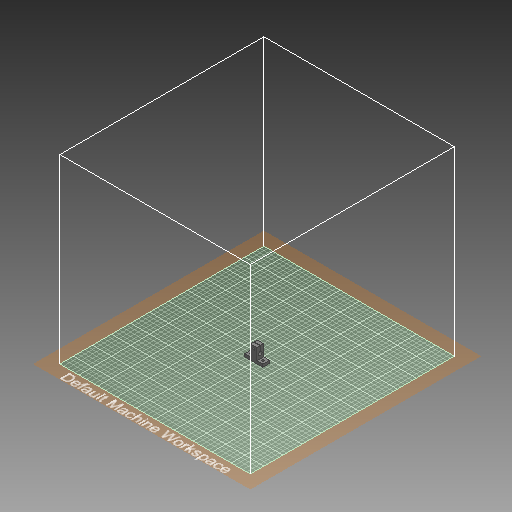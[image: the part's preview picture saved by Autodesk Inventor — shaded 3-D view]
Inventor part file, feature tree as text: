
AUTODESK INVENTOR PART (.ipt)
format: ipt  version: 2019 (Build 230136000, 136)  size: 347,136 bytes
history: native  units: in
note: dims shown in document units (in); Inventor stores cm internally (conversion verified against a paired STEP export)
features: sketch x9, extrude x8, other x3, reference x2
ambient origin geometry x8: Origin, YZ Plane, XZ Plane, XY Plane, X Axis, Y Axis, Z Axis, Center Point
bodies: Solid1 (feature_tree)
feature tree (22):
  extrude  "Extrusion1"  Depth=0.5906in
  extrude  "Extrusion2"  Depth=0.5512in
  extrude  "Extrusion4"  Depth=0.9843in
  extrude  "Extrusion5"  Depth=1.1811in TaperAngle=0.0deg
  extrude  "Extrusion6"  Depth=0.315in
  sketch  "Sketch7"  dims[d18=0.0394in d19=1.1811in d20=0.0in]
  sketch  "Sketch8"  dims[d21=0.1673in d22=0.2362in]
  extrude  "Extrusion8"  Depth=0.0394in TaperAngle=0.0deg
  extrude  "Extrusion9"  Depth=0.2362in
  sketch  "Sketch9"  dims[d23=1.1811in d24=0.0in d25=0.3937in]
  extrude  "Extrusion10"  Depth=0.3937in
  sketch  "Sketch1"  dims[d0=1.5748in d1=0.5906in]
  sketch  "Sketch2"  dims[d2=0.2362in d3=0.0in d4=0.5512in]
  sketch  "Sketch4"  dims[d5=0.9843in d6=0.0in d12=0.1673in]
  sketch  "Sketch5"  dims[d13=0.1673in d14=1.1811in d15=0.0in]
  sketch  "Sketch6"  dims[d16=0.315in d17=0.6299in]
  reference  "Reference1"
  reference  "Reference2"
  sketch  "Sketch10"  dims[d28=0.3937in d29=0.0in d30=0.3937in d31=0.0in d32=0.2362in d33=0.0591in d34=0.0in d35=0.2362in]
  other  "<userpath>\Stuff\Ajedrez2\Ajedrez2.iam"
  other  "Ajedrez2.iam"
  other  "Endstop mecânico - Chave fim de curso:2"
